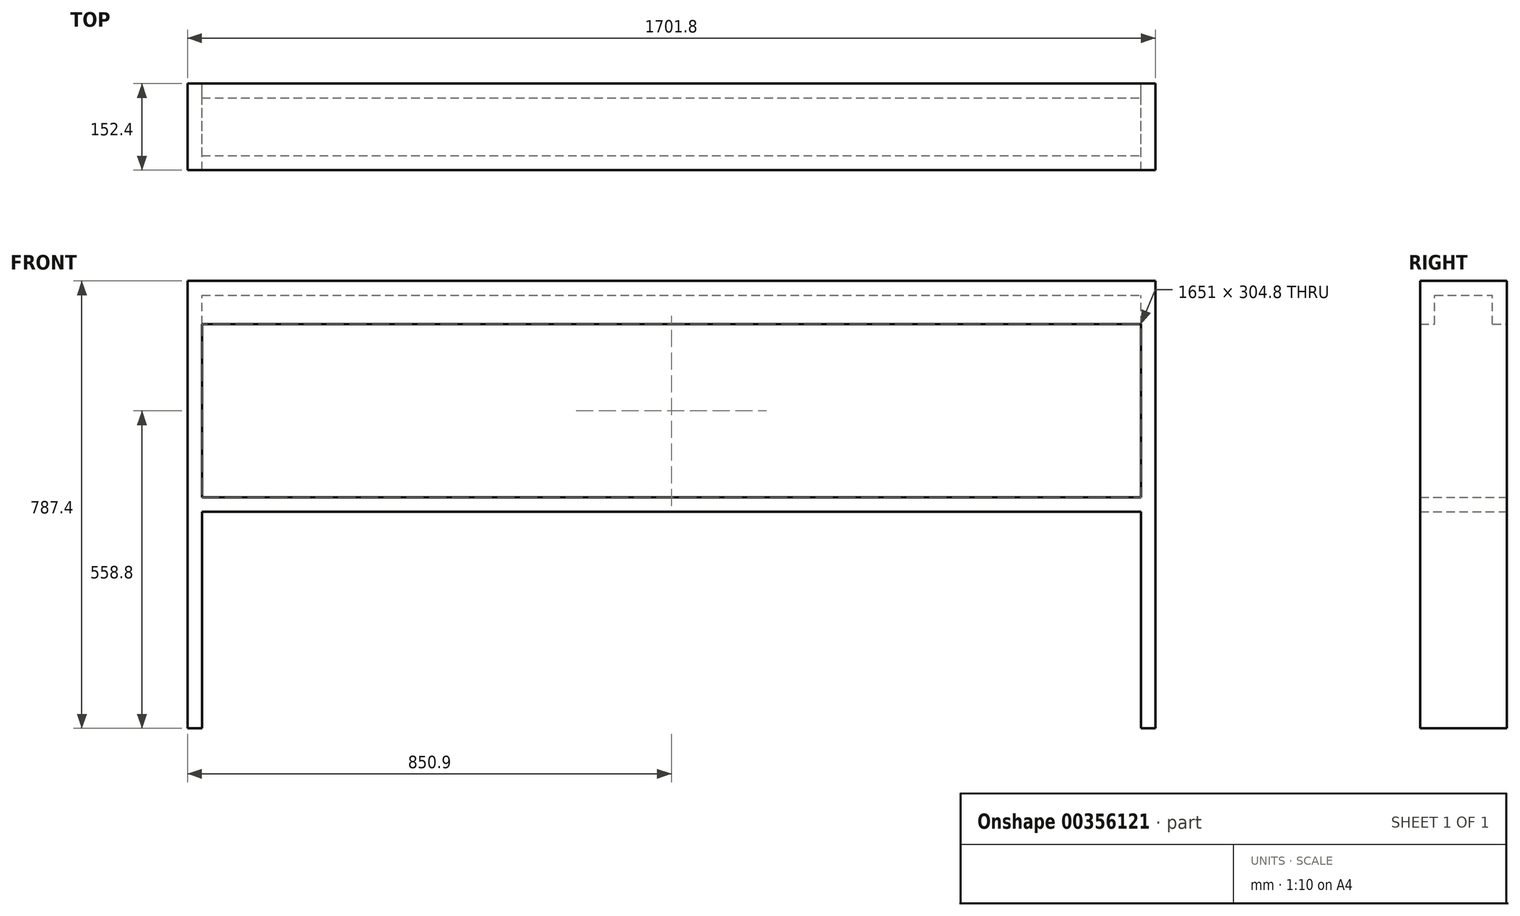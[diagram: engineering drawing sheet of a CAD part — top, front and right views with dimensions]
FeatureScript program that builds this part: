
annotation { "Feature Type Name" : "Feature", "Feature Type Description" : "" }
export const myFeature = defineFeature(function(context is Context, id is Id, definition is map)
    precondition{}
    {
        {
            var Q0;
            Q0=qCreatedBy(makeId("Front.planeOp"),FACE);
            var sketch = newSketch(context, id + "F0", { "sketchPlane" : qUnion([Q0])});
            skLineSegment(sketch, "E0.bottom", {"start": v(-850.9, -393.7) * mm, "end": v(-825.5, -393.7) * mm});
            skLineSegment(sketch, "E0.top", {"start": v(-850.9, 393.7) * mm, "end": v(850.9, 393.7) * mm});
            skLineSegment(sketch, "E0.left", {"start": v(-850.9, -393.7) * mm, "end": v(-850.9, 393.7) * mm});
            skLineSegment(sketch, "E0.right", {"start": v(850.9, -393.7) * mm, "end": v(850.9, 393.7) * mm});
            skPoint(sketch, "E0.middle", {"position": v(0, 0) * mm});
            skLineSegment(sketch, "E1.0", {"start": v(825.5, -393.7) * mm, "end": v(825.5, 368.3) * mm});
            skLineSegment(sketch, "E1.1", {"start": v(-850.9, 368.3) * mm, "end": v(850.9, 368.3) * mm});
            skLineSegment(sketch, "E1.2", {"start": v(-825.5, -393.7) * mm, "end": v(-825.5, 368.3) * mm});
            skLineSegment(sketch, "E2.trimOffspring", {"start": v(825.5, -393.7) * mm, "end": v(850.9, -393.7) * mm});
            skLineSegment(sketch, "E3.0", {"start": v(-825.5, 317.5) * mm, "end": v(825.5, 317.5) * mm});
            skLineSegment(sketch, "E4.bottom", {"start": v(-825.5, 12.7) * mm, "end": v(825.5, 12.7) * mm});
            skLineSegment(sketch, "E4.top", {"start": v(-825.5, -12.7) * mm, "end": v(825.5, -12.7) * mm});
            skLineSegment(sketch, "E4.left", {"start": v(-825.5, 12.7) * mm, "end": v(-825.5, -12.7) * mm});
            skLineSegment(sketch, "E4.right", {"start": v(825.5, 12.7) * mm, "end": v(825.5, -12.7) * mm});
            skSolve(sketch);
        }
        {
            var Q0;
            {var subQ0=sQuery(id+"F0.wireOp",EDGE,"E0.bottom");Q0=makeQuery(id+"F0.imprint","IMPRINT",FACE,{"disambiguationData":[TD([[makeQuery(id+"F0.imprint","IMPRINT",EDGE,{"derivedFrom":subQ0}),1.0]])]});}
            var Q1;
            {var subQ5=sQuery(id+"F0.wireOp",EDGE,"E0.top");Q1=makeQuery(id+"F0.imprint","IMPRINT",FACE,{"disambiguationData":[TD([[makeQuery(id+"F0.imprint","IMPRINT",EDGE,{"derivedFrom":subQ5}),-1.0]])]});}
            var Q2;
            {var subQ4=sQuery(id+"F0.wireOp",EDGE,"E1.0");Q2=makeQuery(id+"F0.imprint","IMPRINT",FACE,{"disambiguationData":[TD([[makeQuery(id+"F0.imprint","IMPRINT",EDGE,{"derivedFrom":subQ4}),-1.0]])]});}
            var Q3;
            Q3=makeQuery(id+"F0.imprint","IMPRINT",FACE,{"disambiguationData":[TD([[makeQuery(id+"F0.imprint","IMPRINT",EDGE,{"derivedFrom":sQuery(id+"F0.wireOp",EDGE,"E4.bottom")}),-1.0]])]});
            extrude(context, id + "F1", {"entities" : qUnion([Q0, Q1, Q2, Q3]), "depth" : 152.4 * mm});
        }
        {
            var Q0;
            {var subQ3=sQuery(id+"F0.wireOp",EDGE,"y4MoqoW9-zOhH-38iE-vI8U-PHhcep3bHATi");Q0=makeQuery(id+"F0.imprint","IMPRINT",FACE,{"disambiguationData":[TD([[makeQuery(id+"F0.imprint","IMPRINT",EDGE,{"derivedFrom":subQ3}),1.0]])]});}
            var Q1;
            {var subQ3=sQuery(id+"F0.wireOp",EDGE,"TbnbpUrM-8pno-Fl90-fRAa-3eZ1riOw7HY4");Q1=makeQuery(id+"F0.imprint","IMPRINT",FACE,{"disambiguationData":[TD([[makeQuery(id+"F0.imprint","IMPRINT",EDGE,{"derivedFrom":subQ3}),1.0]])]});}
            var Q2;
            {var subQ3=sQuery(id+"F0.wireOp",EDGE,"E3.0");Q2=makeQuery(id+"F0.imprint","IMPRINT",FACE,{"disambiguationData":[TD([[makeQuery(id+"F0.imprint","IMPRINT",EDGE,{"derivedFrom":subQ3}),1.0]])]});}
            extrude(context, id + "F2", {"entities" : qUnion([Q0, Q1, Q2]), "operationType" : NewBodyOperationType.ADD, "depth" : 25.4 * mm});
        }
        {
            var Q0;
            Q0=makeQuery(id+"F2.opExtrude","CAP_FACE",FACE,{"disambiguationData":[OSD([sQuery(id+"F0.wireOp",EDGE,"E1.1"),sQuery(id+"F0.wireOp",EDGE,"E1.2"),sQuery(id+"F0.wireOp",EDGE,"y4MoqoW9-zOhH-38iE-vI8U-PHhcep3bHATi")])],"isStart":false});
            var Q1;
            Q1=makeQuery(id+"F2.opExtrude","CAP_FACE",FACE,{"disambiguationData":[OSD([sQuery(id+"F0.wireOp",EDGE,"E1.0"),sQuery(id+"F0.wireOp",EDGE,"E1.1"),sQuery(id+"F0.wireOp",EDGE,"TbnbpUrM-8pno-Fl90-fRAa-3eZ1riOw7HY4")])],"isStart":false});
            extrude(context, id + "F3", {"entities" : qUnion([Q0, Q1]), "operationType" : NewBodyOperationType.ADD, "depth" : 127 * mm, "hasSecondDirection" : true, "secondDirectionOppositeDirection" : false, "secondDirectionDepth" : 101.6 * mm});
        }
    });
